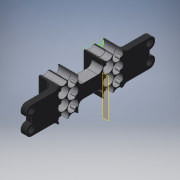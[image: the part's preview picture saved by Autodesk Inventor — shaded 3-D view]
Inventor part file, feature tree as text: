
AUTODESK INVENTOR PART (.ipt)
format: ipt  version: 2016 (Build 200138000, 138)  size: 365,056 bytes
history: native  units: mm
features: other x3, extrude x3, sketch x3, projected_geometry x2, fillet x1, plane x1
ambient origin geometry x8: Origin, YZ Plane, XZ Plane, XY Plane, X Axis, Y Axis, Z Axis, Center Point
bodies: Solid1 (feature_tree)
feature tree (13):
  other  "Main Assembly.iam"
  other  "Motor holder.ipt:1"
  other  "Motor holder.ipt:3"
  extrude  "Extrusion1"  Depth=10.0mm TaperAngle=0.0deg
  extrude  "Extrusion2"  Depth=2.25mm TaperAngle=0.0deg
  extrude  "Extrusion3"  [1 undecoded]
  fillet  "Fillet1"  [1 undecoded]
  plane  "Work Plane1"
  sketch  "Sketch2"  dims[d0=10.0mm d1=10.0mm d2=0.0mm]
  sketch  "Sketch4"  dims[d3=2.25mm d4=0.0mm d5=2.25mm d6=0.0mm]
  projected_geometry  "Projected Loop1"
  sketch  "Sketch5"  dims[d7=2.0mm]
  projected_geometry  "Projected Loop2"
note: 2 required parameter values undecoded (feature->parameter linkage not recoverable at this tier; creation-order binding heuristic only, values carry confidence <= 0.55)
